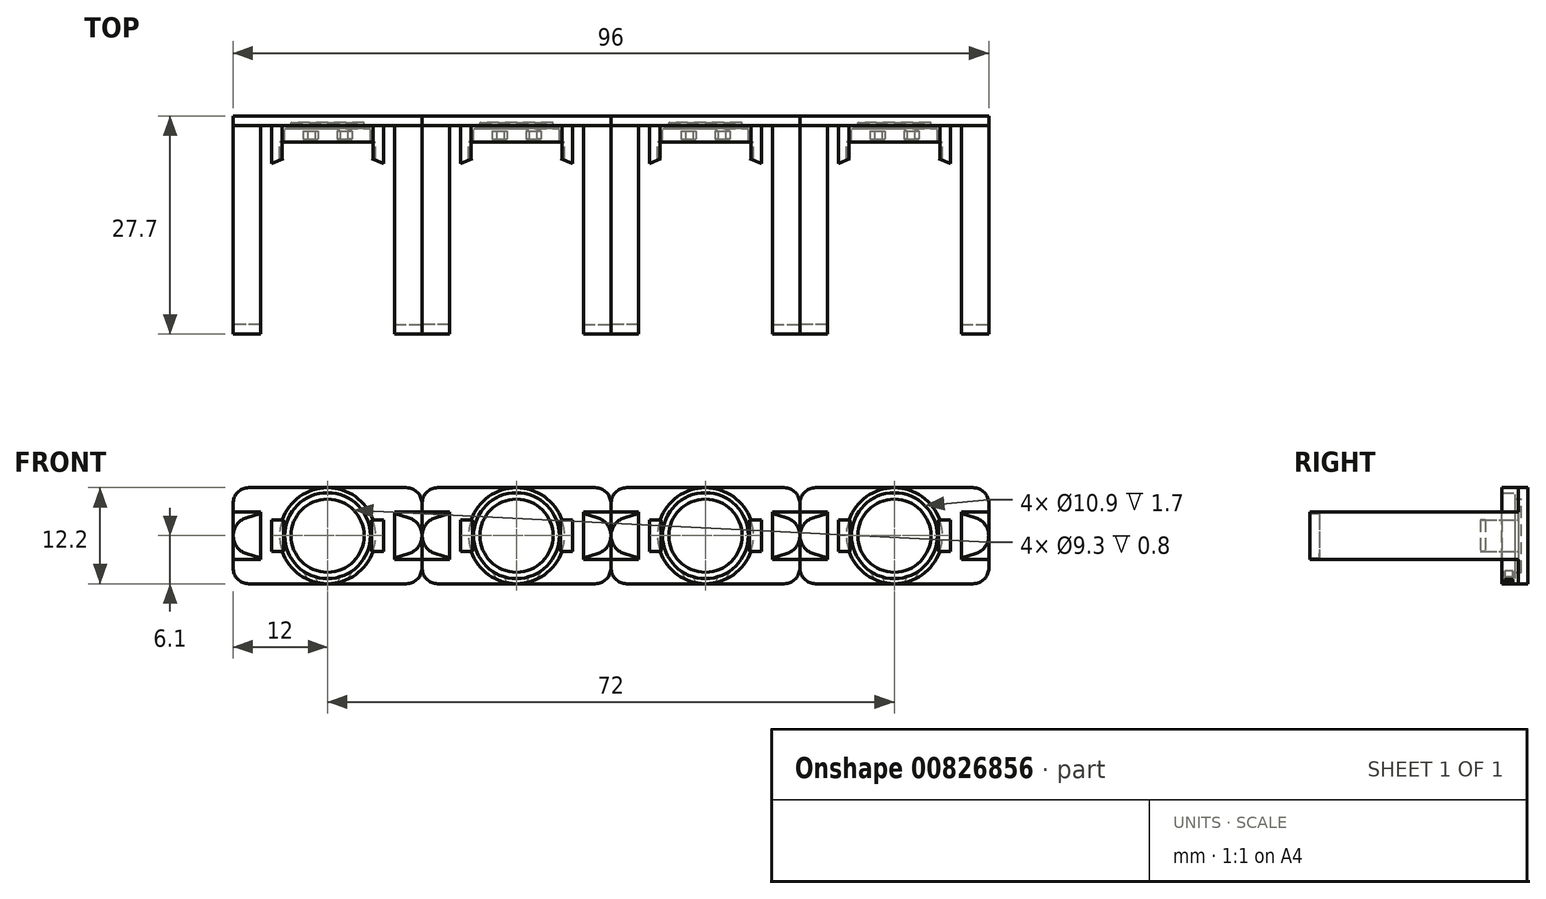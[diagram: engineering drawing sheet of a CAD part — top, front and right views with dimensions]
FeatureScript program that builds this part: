
annotation { "Feature Type Name" : "Feature", "Feature Type Description" : "" }
export const myFeature = defineFeature(function(context is Context, id is Id, definition is map)
    precondition{}
    {
        {
            var Q0;
            Q0=qCreatedBy(makeId("Front.planeOp"),FACE);
            var sketch = newSketch(context, id + "F0", { "sketchPlane" : qUnion([Q0])});
            skCircle(sketch, "E0", {"center": v(0, 0) * mm, "radius": 5 * mm});
            skCircle(sketch, "E1", {"center": v(0, 0) * mm, "radius": 6.1 * mm});
            skSolve(sketch);
        }
        {
            var Q0;
            Q0=makeQuery(id+"F0.imprint","IMPRINT",FACE,{"disambiguationData":[TD([[makeQuery(id+"F0.imprint","IMPRINT",EDGE,{"derivedFrom":sQuery(id+"F0.wireOp",EDGE,"E0")}),-1.0]])]});
            var Q1;
            Q1=makeQuery(id+"F0.imprint","IMPRINT",FACE,{"disambiguationData":[TD([[makeQuery(id+"F0.imprint","IMPRINT",EDGE,{"derivedFrom":sQuery(id+"F0.wireOp",EDGE,"E0")}),1.0]])]});
            extrude(context, id + "F1", {"entities" : qUnion([Q0, Q1]), "depth" : 0.8 * mm, "offsetDistance" : 25 * mm});
        }
        {
            var Q0;
            Q0=makeQuery(id+"F1.opExtrude","CAP_FACE",FACE,{"disambiguationData":[OSD([sQuery(id+"F0.wireOp",EDGE,"E1")])],"isStart":false});
            var sketch = newSketch(context, id + "F2", { "sketchPlane" : qUnion([Q0])});
            skCircle(sketch, "E2", {"center": v(0, 0) * mm, "radius": 5.45 * mm});
            skCircle(sketch, "E3", {"center": v(0, 0) * mm, "radius": 6.1 * mm});
            skSolve(sketch);
        }
        {
            var Q0;
            Q0=makeQuery(id+"F2.imprint","IMPRINT",FACE,{"disambiguationData":[TD([[makeQuery(id+"F2.imprint","IMPRINT",EDGE,{"derivedFrom":sQuery(id+"F2.wireOp",EDGE,"E2")}),-1.0]])]});
            extrude(context, id + "F3", {"entities" : qUnion([Q0]), "operationType" : NewBodyOperationType.ADD, "depth" : 2.5 * mm, "offsetDistance" : 25 * mm});
        }
        {
            var Q0;
            Q0=makeQuery(id+"F1.opExtrude","CAP_FACE",FACE,{"disambiguationData":[OSD([sQuery(id+"F0.wireOp",EDGE,"E1")])],"isStart":false});
            var sketch = newSketch(context, id + "F4", { "sketchPlane" : qUnion([Q0])});
            skCircle(sketch, "E4", {"center": v(0, 0) * mm, "radius": 4.65 * mm});
            skSolve(sketch);
        }
        {
            var Q0;
            Q0=makeQuery(id+"F4.imprint","IMPRINT",FACE,{"disambiguationData":[TD([[makeQuery(id+"F4.imprint","IMPRINT",EDGE,{"derivedFrom":sQuery(id+"F4.wireOp",EDGE,"E4")}),-1.0]])]});
            extrude(context, id + "F5", {"entities" : qUnion([Q0]), "operationType" : NewBodyOperationType.ADD, "depth" : 0.8 * mm, "offsetDistance" : 25 * mm});
        }
        {
            var Q0;
            Q0=makeQuery(id+"F3.opExtrude","CAP_FACE",FACE,{"disambiguationData":[OSD([sQuery(id+"F2.wireOp",EDGE,"E2"),sQuery(id+"F2.wireOp",EDGE,"E3")])],"isStart":false});
            var sketch = newSketch(context, id + "F6", { "sketchPlane" : qUnion([Q0])});
            skLineSegment(sketch, "E5", {"start": v(-1.6, -5.2) * mm, "end": v(-1.2, -5.98) * mm});
            skLineSegment(sketch, "E6", {"start": v(-3.1, -4.48) * mm, "end": v(-2.56, -5.54) * mm});
            skLineSegment(sketch, "E7.MirrorCS", {"start": v(1.6, -5.2) * mm, "end": v(1.2, -5.98) * mm});
            skLineSegment(sketch, "E8.MirrorCS", {"start": v(3.1, -4.48) * mm, "end": v(2.56, -5.54) * mm});
            skSolve(sketch);
        }
        {
            var Q0;
            {var subQ0=sQuery(id+"F6.wireOp",EDGE,"E5");Q0=makeQuery(id+"F6.imprint","IMPRINT",FACE,{"disambiguationData":[TD([[makeQuery(id+"F6.imprint","IMPRINT",EDGE,{"derivedFrom":subQ0}),-1.0]])]});}
            var Q1;
            {var subQ0=sQuery(id+"F6.wireOp",EDGE,"E7.MirrorCS");Q1=makeQuery(id+"F6.imprint","IMPRINT",FACE,{"disambiguationData":[TD([[makeQuery(id+"F6.imprint","IMPRINT",EDGE,{"derivedFrom":subQ0}),1.0]])]});}
            extrude(context, id + "F7", {"entities" : qUnion([Q0, Q1]), "operationType" : NewBodyOperationType.REMOVE, "oppositeDirection" : true, "depth" : 1.4 * mm, "offsetDistance" : 25 * mm});
        }
        {
            var Q0;
            {var subQ0=sQuery(id+"F2.wireOp",EDGE,"E3");var subQ1=sQuery(id+"F2.wireOp",EDGE,"E2");Q0=makeQuery(id+"F7.boolean.opBoolean","SPLIT",FACE,{"disambiguationData":[TD([makeQuery(id+"F7.opExtrude","SWEPT_FACE",FACE,{"disambiguationData":[OSD([sQuery(id+"F6.wireOp",EDGE,"E6")])]})])],"derivedFrom":makeQuery(id+"F3.opExtrude","CAP_FACE",FACE,{"disambiguationData":[OSD([subQ1,subQ0])],"isStart":false})});}
            var sketch = newSketch(context, id + "F8", { "sketchPlane" : qUnion([Q0])});
            skArc(sketch, "E9", {"start": v(-3.1, -4.48) * mm, "mid": v(-2.38, -4.9) * mm, "end": v(-1.6, -5.2) * mm});
            skArc(sketch, "E10", {"start": v(-2.56, -5.54) * mm, "mid": v(-1.9, -5.8) * mm, "end": v(-1.2, -5.98) * mm});
            skLineSegment(sketch, "E11", {"start": v(-3.1, -4.48) * mm, "end": v(-2.56, -5.54) * mm});
            skLineSegment(sketch, "E12", {"start": v(-1.6, -5.2) * mm, "end": v(-1.2, -5.98) * mm});
            skLineSegment(sketch, "E13.MirrorCS", {"start": v(3.1, -4.48) * mm, "end": v(2.56, -5.54) * mm});
            skArc(sketch, "E14.MirrorCS", {"start": v(2.56, -5.54) * mm, "mid": v(1.9, -5.8) * mm, "end": v(1.2, -5.98) * mm});
            skLineSegment(sketch, "E15.MirrorCS", {"start": v(1.6, -5.2) * mm, "end": v(1.2, -5.98) * mm});
            skArc(sketch, "E16.MirrorCS", {"start": v(3.1, -4.48) * mm, "mid": v(2.38, -4.9) * mm, "end": v(1.6, -5.2) * mm});
            skSolve(sketch);
        }
        {
            var Q0;
            Q0=makeQuery(id+"F8.imprint","IMPRINT",FACE,{"disambiguationData":[TD([[makeQuery(id+"F8.imprint","IMPRINT",EDGE,{"derivedFrom":sQuery(id+"F8.wireOp",EDGE,"E9")}),-1.0]])]});
            var Q1;
            Q1=makeQuery(id+"F8.imprint","IMPRINT",FACE,{"disambiguationData":[TD([[makeQuery(id+"F8.imprint","IMPRINT",EDGE,{"derivedFrom":sQuery(id+"F8.wireOp",EDGE,"E13.MirrorCS")}),-1.0]])]});
            extrude(context, id + "F9", {"entities" : qUnion([Q0, Q1]), "operationType" : NewBodyOperationType.ADD, "oppositeDirection" : true, "depth" : 0.4 * mm, "offsetDistance" : 25 * mm});
        }
        {
            var Q0;
            Q0=makeQuery(id+"F1.opExtrude","CAP_FACE",FACE,{"disambiguationData":[OSD([sQuery(id+"F0.wireOp",EDGE,"E1")])],"isStart":true});
            var sketch = newSketch(context, id + "F10", { "sketchPlane" : qUnion([Q0])});
            skLineSegment(sketch, "E17.bottom", {"start": v(-12, -6.1) * mm, "end": v(12, -6.1) * mm});
            skLineSegment(sketch, "E17.top", {"start": v(-12, 6.1) * mm, "end": v(12, 6.1) * mm});
            skLineSegment(sketch, "E17.left", {"start": v(-12, -6.1) * mm, "end": v(-12, 6.1) * mm});
            skLineSegment(sketch, "E17.right", {"start": v(12, -6.1) * mm, "end": v(12, 6.1) * mm});
            skPoint(sketch, "E17.middle", {"position": v(0, 0) * mm});
            skSolve(sketch);
        }
        {
            var Q0;
            {var subQ0=sQuery(id+"F10.wireOp",EDGE,"E17.right");Q0=makeQuery(id+"F10.imprint","IMPRINT",FACE,{"disambiguationData":[TD([[makeQuery(id+"F10.imprint","IMPRINT",EDGE,{"derivedFrom":subQ0}),1.0]])]});}
            var Q1;
            {var subQ0=sQuery(id+"F10.wireOp",EDGE,"E17.left");Q1=makeQuery(id+"F10.imprint","IMPRINT",FACE,{"disambiguationData":[TD([[makeQuery(id+"F10.imprint","IMPRINT",EDGE,{"derivedFrom":subQ0}),-1.0]])]});}
            extrude(context, id + "F11", {"entities" : qUnion([Q0, Q1]), "operationType" : NewBodyOperationType.ADD, "oppositeDirection" : true, "depth" : 1.2 * mm, "offsetDistance" : 25 * mm});
        }
        {
            var Q0;
            Q0=makeQuery(id+"F11.opExtrude","SWEPT_EDGE",EDGE,{"disambiguationData":[OSD([sQuery(id+"F10.wireOp",EDGE,"E17.bottom"),sQuery(id+"F10.wireOp",EDGE,"E17.right")])]});
            var Q1;
            Q1=makeQuery(id+"F11.opExtrude","SWEPT_EDGE",EDGE,{"disambiguationData":[OSD([sQuery(id+"F10.wireOp",EDGE,"E17.bottom"),sQuery(id+"F10.wireOp",EDGE,"E17.left")])]});
            var Q2;
            Q2=makeQuery(id+"F11.opExtrude","SWEPT_EDGE",EDGE,{"disambiguationData":[OSD([sQuery(id+"F10.wireOp",EDGE,"E17.top"),sQuery(id+"F10.wireOp",EDGE,"E17.left")])]});
            var Q3;
            Q3=makeQuery(id+"F11.opExtrude","SWEPT_EDGE",EDGE,{"disambiguationData":[OSD([sQuery(id+"F10.wireOp",EDGE,"E17.top"),sQuery(id+"F10.wireOp",EDGE,"E17.right")])]});
            fillet(context, id + "F12", {"entities" : qUnion([Q0, Q1, Q2, Q3]), "radius" : 2 * mm, "tangentPropagation" : true, "allowEdgeOverflow" : false});
        }
        {
            var Q0;
            Q0=makeQuery(id+"F11.opExtrude","CAP_FACE",FACE,{"disambiguationData":[OSD([sQuery(id+"F0.wireOp",EDGE,"E1"),sQuery(id+"F10.wireOp",EDGE,"E17.bottom"),sQuery(id+"F10.wireOp",EDGE,"E17.top"),sQuery(id+"F10.wireOp",EDGE,"E17.right")])],"isStart":false});
            var sketch = newSketch(context, id + "F13", { "sketchPlane" : qUnion([Q0])});
            skLineSegment(sketch, "E18", {"start": v(-12, 3) * mm, "end": v(-8.5, 3) * mm});
            skLineSegment(sketch, "E19", {"start": v(-8.5, 3) * mm, "end": v(-8.5, -3) * mm});
            skLineSegment(sketch, "E20", {"start": v(-8.5, -3) * mm, "end": v(-12, -3) * mm});
            skLineSegment(sketch, "E21", {"start": v(-7.1, 2) * mm, "end": v(-7.1, -2) * mm});
            skLineSegment(sketch, "E22", {"start": v(-7.1, -2) * mm, "end": v(-5.76, -2) * mm});
            skLineSegment(sketch, "E23", {"start": v(-7.1, 2) * mm, "end": v(-5.76, 2) * mm});
            skSolve(sketch);
        }
        {
            var Q0;
            {var subQ0=sQuery(id+"F13.wireOp",EDGE,"E18");Q0=makeQuery(id+"F13.imprint","IMPRINT",FACE,{"disambiguationData":[TD([[makeQuery(id+"F13.imprint","IMPRINT",EDGE,{"derivedFrom":subQ0}),-1.0]])]});}
            extrude(context, id + "F14", {"entities" : qUnion([Q0]), "operationType" : NewBodyOperationType.ADD, "depth" : 25.3 * mm, "offsetDistance" : 25 * mm});
        }
        {
            var Q0;
            Q0=makeQuery(id+"F11.opExtrude","CAP_FACE",FACE,{"disambiguationData":[OSD([sQuery(id+"F0.wireOp",EDGE,"E1"),sQuery(id+"F10.wireOp",EDGE,"E17.bottom"),sQuery(id+"F10.wireOp",EDGE,"E17.top"),sQuery(id+"F10.wireOp",EDGE,"E17.left")])],"isStart":false});
            var sketch = newSketch(context, id + "F15", { "sketchPlane" : qUnion([Q0])});
            skLineSegment(sketch, "E24", {"start": v(12, 3) * mm, "end": v(8.5, 3) * mm});
            skLineSegment(sketch, "E25", {"start": v(8.5, 3) * mm, "end": v(8.5, -3) * mm});
            skLineSegment(sketch, "E26", {"start": v(8.5, -3) * mm, "end": v(12, -3) * mm});
            skLineSegment(sketch, "E27", {"start": v(7.1, 2) * mm, "end": v(7.1, -2) * mm});
            skLineSegment(sketch, "E28", {"start": v(7.1, -2) * mm, "end": v(5.76, -2) * mm});
            skLineSegment(sketch, "E29", {"start": v(7.1, 2) * mm, "end": v(5.76, 2) * mm});
            skSolve(sketch);
        }
        {
            var Q0;
            {var subQ0=sQuery(id+"F15.wireOp",EDGE,"E24");Q0=makeQuery(id+"F15.imprint","IMPRINT",FACE,{"disambiguationData":[TD([[makeQuery(id+"F15.imprint","IMPRINT",EDGE,{"derivedFrom":subQ0}),1.0]])]});}
            extrude(context, id + "F16", {"entities" : qUnion([Q0]), "operationType" : NewBodyOperationType.ADD, "depth" : 25.3 * mm, "offsetDistance" : 25 * mm});
        }
        {
            var Q0;
            Q0=makeQuery(id+"F15.imprint","IMPRINT",FACE,{"disambiguationData":[TD([[makeQuery(id+"F15.imprint","IMPRINT",EDGE,{"derivedFrom":sQuery(id+"F15.wireOp",EDGE,"E27")}),-1.0]])]});
            var Q1;
            Q1=makeQuery(id+"F13.imprint","IMPRINT",FACE,{"disambiguationData":[TD([[makeQuery(id+"F13.imprint","IMPRINT",EDGE,{"derivedFrom":sQuery(id+"F13.wireOp",EDGE,"E21")}),1.0]])]});
            extrude(context, id + "F17", {"entities" : qUnion([Q0, Q1]), "operationType" : NewBodyOperationType.ADD, "depth" : 4.2 * mm, "offsetDistance" : 25 * mm});
        }
        {
            var Q0;
            Q0=makeQuery(id+"F17.opExtrude","SWEPT_FACE",FACE,{"disambiguationData":[OSD([sQuery(id+"F13.wireOp",EDGE,"E22")])]});
            var sketch = newSketch(context, id + "F18", { "sketchPlane" : qUnion([Q0])});
            skLineSegment(sketch, "E30", {"start": v(-7.1, 5.4) * mm, "end": v(-7.1, 6) * mm});
            skLineSegment(sketch, "E31", {"start": v(-5.76, 5.4) * mm, "end": v(-5.66, 5.4) * mm});
            skLineSegment(sketch, "E32", {"start": v(-5.66, 5.4) * mm, "end": v(-7.1, 6) * mm});
            skSolve(sketch);
        }
        {
            var Q0;
            Q0=makeQuery(id+"F18.imprint","IMPRINT",FACE,{"disambiguationData":[TD([[makeQuery(id+"F18.imprint","IMPRINT",EDGE,{"derivedFrom":sQuery(id+"F18.wireOp",EDGE,"E30")}),-1.0]])]});
            extrude(context, id + "F19", {"entities" : qUnion([Q0]), "operationType" : NewBodyOperationType.ADD, "oppositeDirection" : true, "depth" : 4 * mm, "offsetDistance" : 25 * mm});
        }
        {
            var Q0;
            Q0=makeQuery(id+"F17.opExtrude","SWEPT_FACE",FACE,{"disambiguationData":[OSD([sQuery(id+"F15.wireOp",EDGE,"E28")])]});
            var sketch = newSketch(context, id + "F20", { "sketchPlane" : qUnion([Q0])});
            skLineSegment(sketch, "E33", {"start": v(7.1, 5.4) * mm, "end": v(7.1, 6) * mm});
            skLineSegment(sketch, "E34", {"start": v(5.76, 5.4) * mm, "end": v(5.66, 5.4) * mm});
            skLineSegment(sketch, "E35", {"start": v(5.66, 5.4) * mm, "end": v(7.1, 6) * mm});
            skSolve(sketch);
        }
        {
            var Q0;
            Q0=makeQuery(id+"F20.imprint","IMPRINT",FACE,{"disambiguationData":[TD([[makeQuery(id+"F20.imprint","IMPRINT",EDGE,{"derivedFrom":sQuery(id+"F20.wireOp",EDGE,"E33")}),1.0]])]});
            extrude(context, id + "F21", {"entities" : qUnion([Q0]), "operationType" : NewBodyOperationType.ADD, "oppositeDirection" : true, "depth" : 4 * mm, "offsetDistance" : 25 * mm});
        }
        {
            var Q0;
            {var subQ0=sQuery(id+"F13.wireOp",EDGE,"E22");Q0=makeQuery(id+"F19.boolean.opBoolean","MERGE",FACE,{"derivedFrom":[makeQuery(id+"F17.opExtrude","SWEPT_FACE",FACE,{"disambiguationData":[OSD([subQ0])]}),makeQuery(id+"F19.opExtrude","CAP_FACE",FACE,{"disambiguationData":[OSD([subQ0,sQuery(id+"F18.wireOp",EDGE,"E30"),sQuery(id+"F18.wireOp",EDGE,"scbSYdZa-IKE8-HjIA-PmpS-5iz6sRiiHXsu")])],"isStart":true})]});}
            var sketch = newSketch(context, id + "F22", { "sketchPlane" : qUnion([Q0])});
            skLineSegment(sketch, "E36", {"start": v(-5.76, 5.4) * mm, "end": v(-5.61, 5.4) * mm});
            skLineSegment(sketch, "E37", {"start": v(-5.61, 5.4) * mm, "end": v(-7.1, 6) * mm});
            skSolve(sketch);
        }
        {
            var Q0;
            Q0=makeQuery(id+"F22.imprint","IMPRINT",FACE,{"disambiguationData":[TD([[makeQuery(id+"F22.imprint","IMPRINT",EDGE,{"derivedFrom":sQuery(id+"F22.wireOp",EDGE,"E36")}),1.0]])]});
            extrude(context, id + "F23", {"entities" : qUnion([Q0]), "operationType" : NewBodyOperationType.ADD, "oppositeDirection" : true, "depth" : 4 * mm, "offsetDistance" : 25 * mm});
        }
        {
            var Q0;
            {var subQ0=sQuery(id+"F15.wireOp",EDGE,"E28");Q0=makeQuery(id+"F21.boolean.opBoolean","MERGE",FACE,{"derivedFrom":[makeQuery(id+"F17.opExtrude","SWEPT_FACE",FACE,{"disambiguationData":[OSD([subQ0])]}),makeQuery(id+"F21.opExtrude","CAP_FACE",FACE,{"disambiguationData":[OSD([subQ0,sQuery(id+"F20.wireOp",EDGE,"E33"),sQuery(id+"F20.wireOp",EDGE,"OUZQXp2e-nWsZ-sgYy-KXVV-Yu3MqT17kAb9")])],"isStart":true})]});}
            var sketch = newSketch(context, id + "F24", { "sketchPlane" : qUnion([Q0])});
            skLineSegment(sketch, "E38", {"start": v(5.76, 5.4) * mm, "end": v(5.61, 5.4) * mm});
            skLineSegment(sketch, "E39", {"start": v(5.61, 5.4) * mm, "end": v(7.1, 6) * mm});
            skSolve(sketch);
        }
        {
            var Q0;
            Q0=makeQuery(id+"F24.imprint","IMPRINT",FACE,{"disambiguationData":[TD([[makeQuery(id+"F24.imprint","IMPRINT",EDGE,{"derivedFrom":sQuery(id+"F24.wireOp",EDGE,"E38")}),-1.0]])]});
            extrude(context, id + "F25", {"entities" : qUnion([Q0]), "operationType" : NewBodyOperationType.ADD, "oppositeDirection" : true, "depth" : 4 * mm, "offsetDistance" : 25 * mm});
        }
        {
            var Q0;
            Q0=makeQuery(id+"F16.opExtrude","CAP_FACE",FACE,{"disambiguationData":[OSD([sQuery(id+"F10.wireOp",EDGE,"E17.left"),sQuery(id+"F15.wireOp",EDGE,"E24"),sQuery(id+"F15.wireOp",EDGE,"E25"),sQuery(id+"F15.wireOp",EDGE,"E26")])],"isStart":false});
            var sketch = newSketch(context, id + "F26", { "sketchPlane" : qUnion([Q0])});
            skLineSegment(sketch, "E40", {"start": v(8.5, 2.85) * mm, "end": v(10.35, 2.25) * mm});
            skArc(sketch, "E41", {"start": v(10.35, -2.25) * mm, "mid": v(11.99, 0) * mm, "end": v(10.35, 2.25) * mm});
            skLineSegment(sketch, "E42.MirrorCS", {"start": v(8.5, -2.85) * mm, "end": v(10.35, -2.25) * mm});
            skSolve(sketch);
        }
        {
            var Q0;
            {var subQ2=sQuery(id+"F26.wireOp",EDGE,"E40");Q0=makeQuery(id+"F26.imprint","IMPRINT",FACE,{"disambiguationData":[TD([[makeQuery(id+"F26.imprint","IMPRINT",EDGE,{"derivedFrom":subQ2}),1.0]])]});}
            extrude(context, id + "F27", {"entities" : qUnion([Q0]), "operationType" : NewBodyOperationType.ADD, "depth" : 1.2 * mm, "offsetDistance" : 25 * mm});
        }
        {
            var Q0;
            Q0=makeQuery(id+"F14.opExtrude","CAP_FACE",FACE,{"disambiguationData":[OSD([sQuery(id+"F10.wireOp",EDGE,"E17.right"),sQuery(id+"F13.wireOp",EDGE,"E18"),sQuery(id+"F13.wireOp",EDGE,"E19"),sQuery(id+"F13.wireOp",EDGE,"E20")])],"isStart":false});
            var sketch = newSketch(context, id + "F28", { "sketchPlane" : qUnion([Q0])});
            skLineSegment(sketch, "E43", {"start": v(-8.5, 2.85) * mm, "end": v(-10.35, 2.25) * mm});
            skLineSegment(sketch, "E44.MirrorCS", {"start": v(-8.5, -2.85) * mm, "end": v(-10.35, -2.25) * mm});
            skArc(sketch, "E45", {"start": v(-10.35, 2.25) * mm, "mid": v(-12, 0) * mm, "end": v(-10.35, -2.25) * mm});
            skSolve(sketch);
        }
        {
            var Q0;
            {var subQ2=sQuery(id+"F28.wireOp",EDGE,"E43");Q0=makeQuery(id+"F28.imprint","IMPRINT",FACE,{"disambiguationData":[TD([[makeQuery(id+"F28.imprint","IMPRINT",EDGE,{"derivedFrom":subQ2}),-1.0]])]});}
            extrude(context, id + "F29", {"entities" : qUnion([Q0]), "operationType" : NewBodyOperationType.ADD, "depth" : 1.2 * mm, "offsetDistance" : 25 * mm});
        }
        {
            var Q0;
            Q0=makeQuery(id+"F1.opExtrude","SWEPT_BODY",BODY,{"disambiguationData":[OSD([sQuery(id+"F0.wireOp",EDGE,"E1")])]});
            var Q1;
            Q1=sQuery(id+"F10.wireOp",EDGE,"E17.top");
            transform(context, id + "F30", {"entities" : qUnion([Q0]), "transformType" : TransformType.TRANSLATION_ENTITY, "oppositeDirectionEntity" : false, "transformLine" : qUnion([Q1]), "makeCopy" : true});
        }
        {
            var Q0;
            Q0=makeQuery(id+"F1.opExtrude","SWEPT_BODY",BODY,{"disambiguationData":[OSD([sQuery(id+"F0.wireOp",EDGE,"E1")])]});
            var Q1;
            Q1=sQuery(id+"F10.wireOp",EDGE,"E17.top");
            transform(context, id + "F31", {"entities" : qUnion([Q0]), "transformType" : TransformType.TRANSLATION_DISTANCE, "transformDirection" : qUnion([Q1]), "distance" : 48 * mm, "makeCopy" : true});
        }
        {
            var Q0;
            Q0=makeQuery(id+"F1.opExtrude","SWEPT_BODY",BODY,{"disambiguationData":[OSD([sQuery(id+"F0.wireOp",EDGE,"E1")])]});
            var Q1;
            Q1=sQuery(id+"F10.wireOp",EDGE,"E17.top");
            transform(context, id + "F32", {"entities" : qUnion([Q0]), "transformType" : TransformType.TRANSLATION_DISTANCE, "transformDirection" : qUnion([Q1]), "distance" : 72 * mm, "makeCopy" : true});
        }
    });
